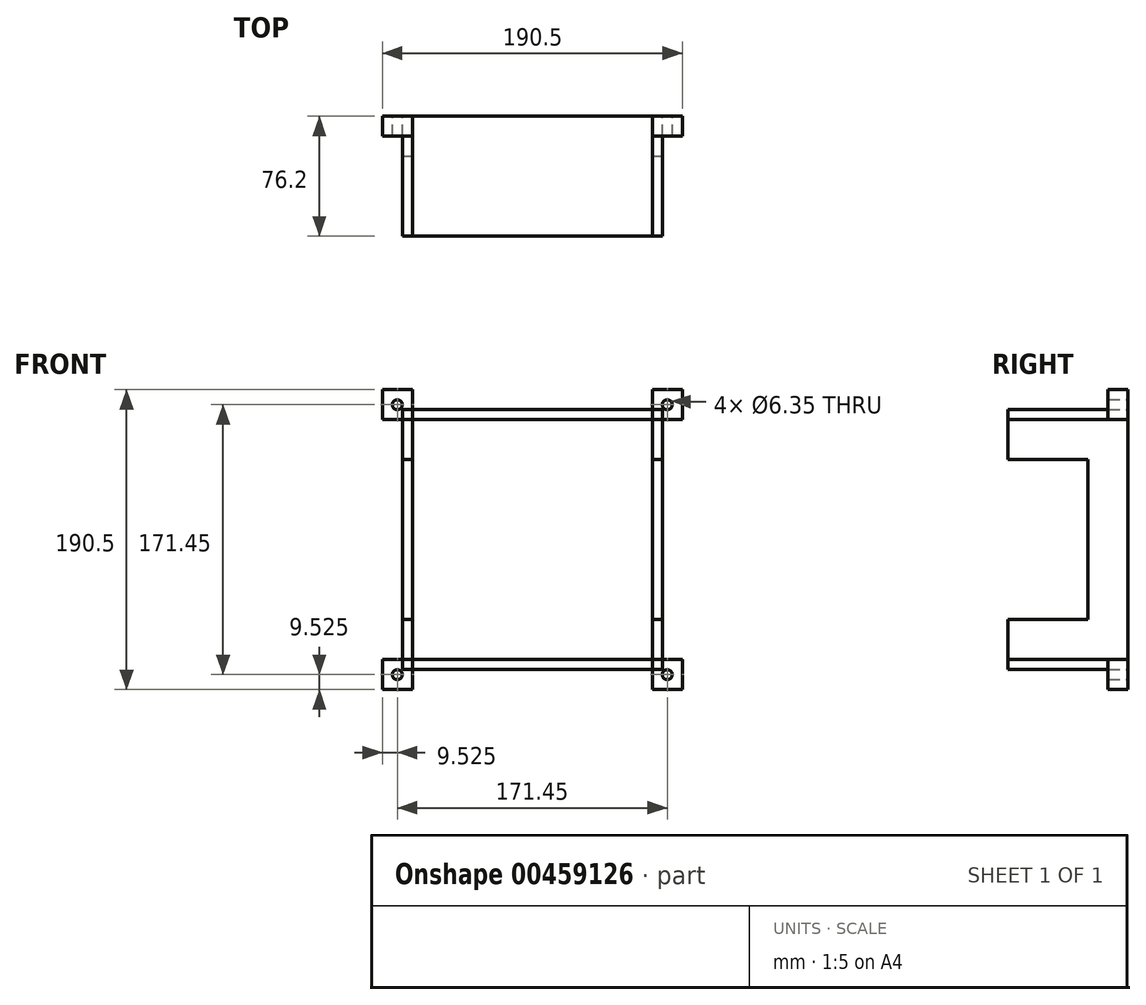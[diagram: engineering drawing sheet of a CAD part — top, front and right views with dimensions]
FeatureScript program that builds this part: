
annotation { "Feature Type Name" : "Feature", "Feature Type Description" : "" }
export const myFeature = defineFeature(function(context is Context, id is Id, definition is map)
    precondition{}
    {
        {
            var Q0;
            Q0=qCreatedBy(makeId("Front.planeOp"),FACE);
            var sketch = newSketch(context, id + "F0", { "sketchPlane" : qUnion([Q0])});
            skLineSegment(sketch, "E0.bottom", {"start": v(-76.2, 76.2) * mm, "end": v(76.2, 76.2) * mm});
            skLineSegment(sketch, "E0.top", {"start": v(-76.2, -76.2) * mm, "end": v(76.2, -76.2) * mm});
            skLineSegment(sketch, "E0.left", {"start": v(-76.2, 76.2) * mm, "end": v(-76.2, -76.2) * mm});
            skLineSegment(sketch, "E0.right", {"start": v(76.2, 76.2) * mm, "end": v(76.2, -76.2) * mm});
            skPoint(sketch, "E0.middle", {"position": v(0, 0) * mm});
            skLineSegment(sketch, "E1.bottom", {"start": v(-82.55, 82.55) * mm, "end": v(82.55, 82.55) * mm});
            skLineSegment(sketch, "E1.top", {"start": v(-82.55, -82.55) * mm, "end": v(82.55, -82.55) * mm});
            skLineSegment(sketch, "E1.left", {"start": v(-82.55, 82.55) * mm, "end": v(-82.55, -82.55) * mm});
            skLineSegment(sketch, "E1.right", {"start": v(82.55, 82.55) * mm, "end": v(82.55, -82.55) * mm});
            skLineSegment(sketch, "E2.bottom", {"start": v(-76.2, 76.2) * mm, "end": v(-95.25, 76.2) * mm});
            skLineSegment(sketch, "E2.top", {"start": v(-76.2, 95.25) * mm, "end": v(-95.25, 95.25) * mm});
            skLineSegment(sketch, "E2.left", {"start": v(-76.2, 76.2) * mm, "end": v(-76.2, 95.25) * mm});
            skLineSegment(sketch, "E2.right", {"start": v(-95.25, 76.2) * mm, "end": v(-95.25, 95.25) * mm});
            skLineSegment(sketch, "E3.bottom", {"start": v(76.2, 76.2) * mm, "end": v(95.25, 76.2) * mm});
            skLineSegment(sketch, "E3.top", {"start": v(76.2, 95.25) * mm, "end": v(95.25, 95.25) * mm});
            skLineSegment(sketch, "E3.left", {"start": v(76.2, 76.2) * mm, "end": v(76.2, 95.25) * mm});
            skLineSegment(sketch, "E3.right", {"start": v(95.25, 76.2) * mm, "end": v(95.25, 95.25) * mm});
            skLineSegment(sketch, "E4.MirrorCS", {"start": v(95.25, -76.2) * mm, "end": v(95.25, -95.25) * mm});
            skLineSegment(sketch, "E5.MirrorCS", {"start": v(76.2, -95.25) * mm, "end": v(95.25, -95.25) * mm});
            skLineSegment(sketch, "E6.MirrorCS", {"start": v(76.2, -76.2) * mm, "end": v(76.2, -95.25) * mm});
            skLineSegment(sketch, "E7.MirrorCS", {"start": v(76.2, -76.2) * mm, "end": v(95.25, -76.2) * mm});
            skLineSegment(sketch, "E8.MirrorCS", {"start": v(-76.2, -76.2) * mm, "end": v(-95.25, -76.2) * mm});
            skLineSegment(sketch, "E9.MirrorCS", {"start": v(-95.25, -76.2) * mm, "end": v(-95.25, -95.25) * mm});
            skLineSegment(sketch, "E10.MirrorCS", {"start": v(-76.2, -95.25) * mm, "end": v(-95.25, -95.25) * mm});
            skLineSegment(sketch, "E11.MirrorCS", {"start": v(-76.2, -76.2) * mm, "end": v(-76.2, -95.25) * mm});
            skCircle(sketch, "E12", {"center": v(85.73, 85.72) * mm, "radius": 3.18 * mm});
            skCircle(sketch, "E13.MirrorC", {"center": v(-85.73, 85.72) * mm, "radius": 3.18 * mm});
            skCircle(sketch, "E14.MirrorC", {"center": v(85.73, -85.72) * mm, "radius": 3.18 * mm});
            skCircle(sketch, "E15.MirrorC", {"center": v(-85.73, -85.72) * mm, "radius": 3.18 * mm});
            skSolve(sketch);
        }
        {
            var Q0;
            {var subQ0=sQuery(id+"F0.wireOp",EDGE,"E0.bottom");Q0=makeQuery(id+"F0.imprint","IMPRINT",FACE,{"disambiguationData":[TD([[makeQuery(id+"F0.imprint","IMPRINT",EDGE,{"derivedFrom":subQ0}),1.0]])]});}
            var Q1;
            {var subQ0=sQuery(id+"F0.wireOp",EDGE,"E0.left");Q1=makeQuery(id+"F0.imprint","IMPRINT",FACE,{"disambiguationData":[TD([[makeQuery(id+"F0.imprint","IMPRINT",EDGE,{"derivedFrom":subQ0}),-1.0]])]});}
            var Q2;
            {var subQ0=sQuery(id+"F0.wireOp",EDGE,"E0.right");Q2=makeQuery(id+"F0.imprint","IMPRINT",FACE,{"disambiguationData":[TD([[makeQuery(id+"F0.imprint","IMPRINT",EDGE,{"derivedFrom":subQ0}),1.0]])]});}
            var Q3;
            {var subQ0=sQuery(id+"F0.wireOp",EDGE,"E0.top");Q3=makeQuery(id+"F0.imprint","IMPRINT",FACE,{"disambiguationData":[TD([[makeQuery(id+"F0.imprint","IMPRINT",EDGE,{"derivedFrom":subQ0}),-1.0]])]});}
            extrude(context, id + "F1", {"entities" : qUnion([Q0, Q1, Q2, Q3]), "depth" : 76.2 * mm});
        }
        {
            var Q0;
            Q0=makeQuery(id+"F0.imprint","IMPRINT",FACE,{"disambiguationData":[TD([[makeQuery(id+"F0.imprint","IMPRINT",EDGE,{"derivedFrom":sQuery(id+"F0.wireOp",EDGE,"E0.top")}),-1.0]])]});
            extrude(context, id + "F2", {"entities" : qUnion([Q0]), "operationType" : NewBodyOperationType.ADD, "depth" : 25.4 * mm});
        }
        {
            var Q0;
            Q0=makeQuery(id+"F1.opExtrude","SWEPT_FACE",FACE,{"disambiguationData":[OSD([sQuery(id+"F0.wireOp",EDGE,"E1.right")])]});
            var sketch = newSketch(context, id + "F3", { "sketchPlane" : qUnion([Q0])});
            skLineSegment(sketch, "E16.bottom", {"start": v(-76.2, 50.8) * mm, "end": v(-25.4, 50.8) * mm});
            skLineSegment(sketch, "E16.top", {"start": v(-76.2, -50.8) * mm, "end": v(-25.4, -50.8) * mm});
            skLineSegment(sketch, "E16.left", {"start": v(-76.2, 50.8) * mm, "end": v(-76.2, -50.8) * mm});
            skLineSegment(sketch, "E17.bottom", {"start": v(-76.2, 82.55) * mm, "end": v(-70.36, 82.55) * mm});
            skLineSegment(sketch, "E17.left", {"start": v(-76.2, 82.55) * mm, "end": v(-76.2, 50.8) * mm});
            skLineSegment(sketch, "E18.bottom", {"start": v(-25.4, -50.8) * mm, "end": v(-76.2, -50.8) * mm});
            skLineSegment(sketch, "E18.top", {"start": v(-70.36, -82.55) * mm, "end": v(-76.2, -82.55) * mm});
            skLineSegment(sketch, "E18.right", {"start": v(-76.2, -50.8) * mm, "end": v(-76.2, -82.55) * mm});
            skLineSegment(sketch, "E19", {"start": v(-25.4, 50.8) * mm, "end": v(-25.4, -50.8) * mm});
            skSolve(sketch);
        }
        {
            var Q0;
            Q0=makeQuery(id+"F3.imprint","IMPRINT",FACE,{"disambiguationData":[TD([[makeQuery(id+"F3.imprint","IMPRINT",EDGE,{"derivedFrom":sQuery(id+"F3.wireOp",EDGE,"E16.left")}),1.0]])]});
            extrude(context, id + "F4", {"entities" : qUnion([Q0]), "operationType" : NewBodyOperationType.REMOVE, "oppositeDirection" : true, "depth" : 254 * mm});
        }
        {
            var Q0;
            {var subQ0=sQuery(id+"F0.wireOp",EDGE,"E2.top");Q0=makeQuery(id+"F0.imprint","IMPRINT",FACE,{"disambiguationData":[TD([[makeQuery(id+"F0.imprint","IMPRINT",EDGE,{"derivedFrom":subQ0}),1.0]])]});}
            var Q1;
            {var subQ0=sQuery(id+"F0.wireOp",EDGE,"E3.top");Q1=makeQuery(id+"F0.imprint","IMPRINT",FACE,{"disambiguationData":[TD([[makeQuery(id+"F0.imprint","IMPRINT",EDGE,{"derivedFrom":subQ0}),-1.0]])]});}
            var Q2;
            {var subQ0=sQuery(id+"F0.wireOp",EDGE,"E4.MirrorCS");Q2=makeQuery(id+"F0.imprint","IMPRINT",FACE,{"disambiguationData":[TD([[makeQuery(id+"F0.imprint","IMPRINT",EDGE,{"derivedFrom":subQ0}),-1.0]])]});}
            var Q3;
            {var subQ0=sQuery(id+"F0.wireOp",EDGE,"E9.MirrorCS");Q3=makeQuery(id+"F0.imprint","IMPRINT",FACE,{"disambiguationData":[TD([[makeQuery(id+"F0.imprint","IMPRINT",EDGE,{"derivedFrom":subQ0}),1.0]])]});}
            extrude(context, id + "F5", {"entities" : qUnion([Q0, Q1, Q2, Q3]), "depth" : 12.7 * mm});
        }
        {
            var Q0;
            {var subQ0=sQuery(id+"F0.wireOp",EDGE,"E1.left");var subQ1=sQuery(id+"F0.wireOp",EDGE,"E1.bottom");var subQ2=makeQuery(id+"F0.imprint","INTERSECT",VERTEX,{"derivedFrom":[subQ1,subQ0]});Q0=makeQuery(id+"F0.imprint","IMPRINT",FACE,{"disambiguationData":[TD([[makeQuery(id+"F0.imprint","IMPRINT",EDGE,{"disambiguationData":[TD([[subQ2,-1.0]])],"derivedFrom":subQ1}),-1.0]])]});}
            var Q1;
            {var subQ0=sQuery(id+"F0.wireOp",EDGE,"E1.right");var subQ1=sQuery(id+"F0.wireOp",EDGE,"E1.bottom");var subQ2=makeQuery(id+"F0.imprint","INTERSECT",VERTEX,{"derivedFrom":[subQ1,subQ0]});Q1=makeQuery(id+"F0.imprint","IMPRINT",FACE,{"disambiguationData":[TD([[makeQuery(id+"F0.imprint","IMPRINT",EDGE,{"disambiguationData":[TD([[subQ2,1.0]])],"derivedFrom":subQ1}),-1.0]])]});}
            var Q2;
            {var subQ0=sQuery(id+"F0.wireOp",EDGE,"E1.left");var subQ1=sQuery(id+"F0.wireOp",EDGE,"E1.top");var subQ2=makeQuery(id+"F0.imprint","INTERSECT",VERTEX,{"derivedFrom":[subQ1,subQ0]});Q2=makeQuery(id+"F0.imprint","IMPRINT",FACE,{"disambiguationData":[TD([[makeQuery(id+"F0.imprint","IMPRINT",EDGE,{"disambiguationData":[TD([[subQ2,-1.0]])],"derivedFrom":subQ1}),1.0]])]});}
            var Q3;
            {var subQ0=sQuery(id+"F0.wireOp",EDGE,"E1.right");var subQ1=sQuery(id+"F0.wireOp",EDGE,"E1.top");var subQ2=makeQuery(id+"F0.imprint","INTERSECT",VERTEX,{"derivedFrom":[subQ1,subQ0]});Q3=makeQuery(id+"F0.imprint","IMPRINT",FACE,{"disambiguationData":[TD([[makeQuery(id+"F0.imprint","IMPRINT",EDGE,{"disambiguationData":[TD([[subQ2,1.0]])],"derivedFrom":subQ1}),1.0]])]});}
            extrude(context, id + "F6", {"entities" : qUnion([Q0, Q1, Q2, Q3]), "depth" : 76.2 * mm});
        }
        {
            var Q0;
            Q0=makeQuery(id+"F0.imprint","IMPRINT",FACE,{"disambiguationData":[TD([[makeQuery(id+"F0.imprint","IMPRINT",EDGE,{"derivedFrom":sQuery(id+"F0.wireOp",EDGE,"E12")}),1.0]])]});
            var Q1;
            Q1=makeQuery(id+"F0.imprint","IMPRINT",FACE,{"disambiguationData":[TD([[makeQuery(id+"F0.imprint","IMPRINT",EDGE,{"derivedFrom":sQuery(id+"F0.wireOp",EDGE,"E13.MirrorC")}),-1.0]])]});
            var Q2;
            {var subQ0=sQuery(id+"F0.wireOp",EDGE,"E9.MirrorCS");Q2=makeQuery(id+"F0.imprint","IMPRINT",FACE,{"disambiguationData":[TD([[makeQuery(id+"F0.imprint","IMPRINT",EDGE,{"derivedFrom":subQ0}),1.0]])]});}
            var Q3;
            Q3=makeQuery(id+"F0.imprint","IMPRINT",FACE,{"disambiguationData":[TD([[makeQuery(id+"F0.imprint","IMPRINT",EDGE,{"derivedFrom":sQuery(id+"F0.wireOp",EDGE,"E14.MirrorC")}),-1.0]])]});
            extrude(context, id + "F7", {"entities" : qUnion([Q0, Q1, Q2, Q3]), "operationType" : NewBodyOperationType.REMOVE, "oppositeDirection" : true, "depth" : 12.7 * mm});
        }
    });
